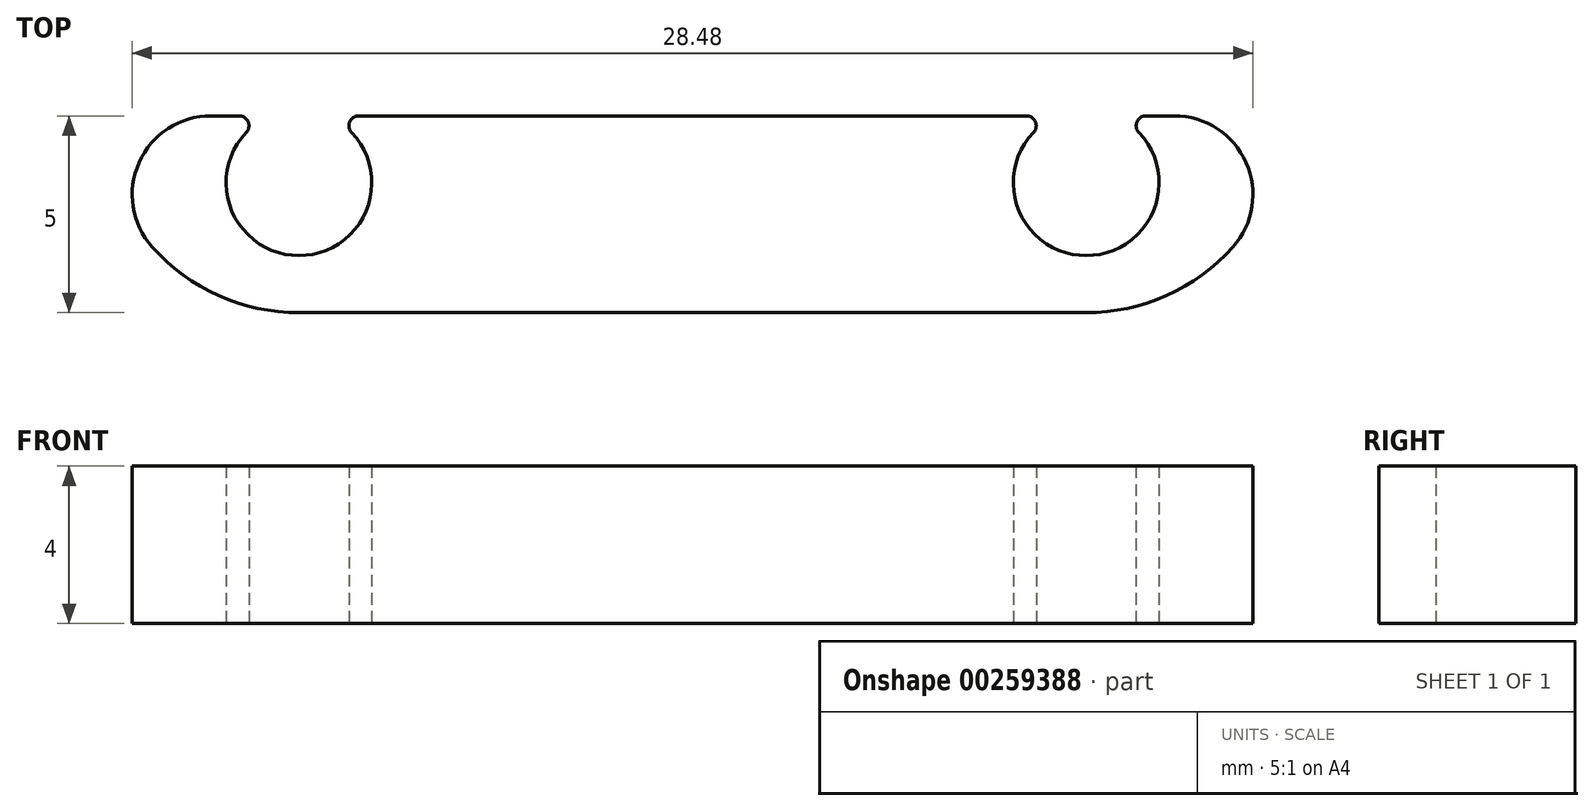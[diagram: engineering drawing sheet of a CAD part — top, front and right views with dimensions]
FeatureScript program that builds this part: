
annotation { "Feature Type Name" : "Feature", "Feature Type Description" : "" }
export const myFeature = defineFeature(function(context is Context, id is Id, definition is map)
    precondition{}
    {
        {
            var Q0;
            Q0=qCreatedBy(makeId("Top.planeOp"),FACE);
            var sketch = newSketch(context, id + "F0", { "sketchPlane" : qUnion([Q0])});
            skLineSegment(sketch, "E0.bottom", {"start": v(-15, 2.5) * mm, "end": v(15, 2.5) * mm});
            skLineSegment(sketch, "E0.top", {"start": v(-15, -2.5) * mm, "end": v(15, -2.5) * mm});
            skLineSegment(sketch, "E0.left", {"start": v(-15, 2.5) * mm, "end": v(-15, -2.5) * mm});
            skLineSegment(sketch, "E0.right", {"start": v(15, 2.5) * mm, "end": v(15, -2.5) * mm});
            skPoint(sketch, "E0.middle", {"position": v(0, 0) * mm});
            skLineSegment(sketch, "E1", {"start": v(-15, 0.8) * mm, "end": v(15, 0.8) * mm, "construction": true});
            skCircle(sketch, "E2", {"center": v(-10, 0.8) * mm, "radius": 1.85 * mm});
            skCircle(sketch, "E3", {"center": v(10, 0.8) * mm, "radius": 1.85 * mm});
            skSolve(sketch);
        }
        {
            var Q0;
            Q0=makeQuery(id+"F0.imprint","IMPRINT",FACE,{"disambiguationData":[TD([[makeQuery(id+"F0.imprint","IMPRINT",EDGE,{"derivedFrom":sQuery(id+"F0.wireOp",EDGE,"E0.top")}),1.0]])]});
            extrude(context, id + "F1", {"entities" : qUnion([Q0]), "depth" : 4 * mm});
        }
        {
            var Q0;
            Q0=makeQuery(id+"F1.opExtrude","SWEPT_EDGE",EDGE,{"disambiguationData":[OSD([sQuery(id+"F0.wireOp",EDGE,"E0.top"),sQuery(id+"F0.wireOp",EDGE,"E0.right")])]});
            var Q1;
            Q1=makeQuery(id+"F1.opExtrude","SWEPT_EDGE",EDGE,{"disambiguationData":[OSD([sQuery(id+"F0.wireOp",EDGE,"E0.top"),sQuery(id+"F0.wireOp",EDGE,"E0.left")])]});
            fillet(context, id + "F2", {"entities" : qUnion([Q0, Q1]), "radius" : 5 * mm, "tangentPropagation" : true, "allowEdgeOverflow" : false});
        }
        {
            var Q0;
            {var subQ0=sQuery(id+"F0.wireOp",EDGE,"E0.right");var subQ1=sQuery(id+"F0.wireOp",EDGE,"E0.bottom");Q0=makeQuery(id+"F2.opFillet","BLEND_EDGE",EDGE,{"blendedFrom":[makeQuery(id+"F1.opExtrude","SWEPT_EDGE",EDGE,{"disambiguationData":[OSD([sQuery(id+"F0.wireOp",EDGE,"E0.top"),subQ0])]}),makeQuery(id+"F1.opExtrude","SWEPT_FACE",FACE,{"disambiguationData":[OSD([subQ1]),TDD([makeQuery(id+"F0.imprint","IMPRINT",EDGE,{"disambiguationData":[TD([[makeQuery(id+"F0.imprint","INTERSECT",VERTEX,{"derivedFrom":[subQ1,subQ0]}),1.0]])],"derivedFrom":subQ1})])]})],"blendedInto":[makeQuery(id+"F1.opExtrude","SWEPT_FACE",FACE,{"disambiguationData":[OSD([subQ1]),TDD([makeQuery(id+"F0.imprint","IMPRINT",EDGE,{"disambiguationData":[TD([[makeQuery(id+"F0.imprint","INTERSECT",VERTEX,{"derivedFrom":[subQ1,subQ0]}),1.0]])],"derivedFrom":subQ1})])]})]});}
            var Q1;
            {var subQ0=sQuery(id+"F0.wireOp",EDGE,"E0.left");var subQ1=sQuery(id+"F0.wireOp",EDGE,"E0.bottom");Q1=makeQuery(id+"F2.opFillet","BLEND_EDGE",EDGE,{"blendedFrom":[makeQuery(id+"F1.opExtrude","SWEPT_EDGE",EDGE,{"disambiguationData":[OSD([sQuery(id+"F0.wireOp",EDGE,"E0.top"),subQ0])]}),makeQuery(id+"F1.opExtrude","SWEPT_FACE",FACE,{"disambiguationData":[OSD([subQ1]),TDD([makeQuery(id+"F0.imprint","IMPRINT",EDGE,{"disambiguationData":[TD([[makeQuery(id+"F0.imprint","INTERSECT",VERTEX,{"derivedFrom":[subQ1,subQ0]}),-1.0]])],"derivedFrom":subQ1})])]})],"blendedInto":[makeQuery(id+"F1.opExtrude","SWEPT_FACE",FACE,{"disambiguationData":[OSD([subQ1]),TDD([makeQuery(id+"F0.imprint","IMPRINT",EDGE,{"disambiguationData":[TD([[makeQuery(id+"F0.imprint","INTERSECT",VERTEX,{"derivedFrom":[subQ1,subQ0]}),-1.0]])],"derivedFrom":subQ1})])]})]});}
            fillet(context, id + "F3", {"entities" : qUnion([Q0, Q1]), "radius" : 2 * mm, "tangentPropagation" : true, "allowEdgeOverflow" : false});
        }
        {
            var Q0;
            {var subQ0=sQuery(id+"F0.wireOp",EDGE,"E3");var subQ1=sQuery(id+"F0.wireOp",EDGE,"E0.bottom");Q0=makeQuery(id+"F1.opExtrude","SWEPT_EDGE",EDGE,{"disambiguationData":[OSD([subQ1,subQ0]),TDD([makeQuery(id+"F0.imprint","INTERSECT",VERTEX,{"disambiguationData":[OD(0.0)],"derivedFrom":[subQ1,subQ0]})])]});}
            var Q1;
            {var subQ0=sQuery(id+"F0.wireOp",EDGE,"E3");var subQ1=sQuery(id+"F0.wireOp",EDGE,"E0.bottom");Q1=makeQuery(id+"F1.opExtrude","SWEPT_EDGE",EDGE,{"disambiguationData":[OSD([subQ1,subQ0]),TDD([makeQuery(id+"F0.imprint","INTERSECT",VERTEX,{"disambiguationData":[OD(1.0)],"derivedFrom":[subQ1,subQ0]})])]});}
            var Q2;
            {var subQ0=sQuery(id+"F0.wireOp",EDGE,"E2");var subQ1=sQuery(id+"F0.wireOp",EDGE,"E0.bottom");Q2=makeQuery(id+"F1.opExtrude","SWEPT_EDGE",EDGE,{"disambiguationData":[OSD([subQ1,subQ0]),TDD([makeQuery(id+"F0.imprint","INTERSECT",VERTEX,{"disambiguationData":[OD(1.0)],"derivedFrom":[subQ1,subQ0]})])]});}
            var Q3;
            {var subQ0=sQuery(id+"F0.wireOp",EDGE,"E2");var subQ1=sQuery(id+"F0.wireOp",EDGE,"E0.bottom");Q3=makeQuery(id+"F1.opExtrude","SWEPT_EDGE",EDGE,{"disambiguationData":[OSD([subQ1,subQ0]),TDD([makeQuery(id+"F0.imprint","INTERSECT",VERTEX,{"disambiguationData":[OD(0.0)],"derivedFrom":[subQ1,subQ0]})])]});}
            fillet(context, id + "F4", {"entities" : qUnion([Q0, Q1, Q2, Q3]), "radius" : 0.25 * mm, "tangentPropagation" : true, "allowEdgeOverflow" : false});
        }
    });
